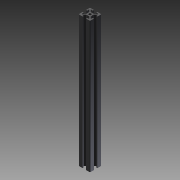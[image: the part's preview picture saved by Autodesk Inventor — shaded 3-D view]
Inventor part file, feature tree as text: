
AUTODESK INVENTOR PART (.ipt)
format: ipt  version: 2011 SP1 (Build 150282100, 282)  size: 185,344 bytes
history: native  units: mm
features: other x7, sketch x2, extrude x1, hole x1
ambient origin geometry x8: Origin, YZ Plane, XZ Plane, XY Plane, X Axis, Y Axis, Z Axis, Center Point
bodies: Solid1 (feature_tree)
feature tree (11):
  extrude  "Extrusion1"  TaperAngle=0.0deg  [1 undecoded]
  hole  "Hole1"  [1 undecoded]
  other  "C1_XY"
  other  "C1_YZ"
  other  "C1_ZX"
  other  "C1_X"
  other  "C1_Y"
  other  "C1_Z"
  other  "C1_Center"
  sketch  "Sketch_75"  dims[d2=4.2mm d3=6.0mm d4=4.0mm d5=2.0mm d6=90.0deg d7=230.0mm d8=0.0mm d9=0.0mm]
  sketch  "Sketch2"  dims[d0=230.0mm d1=0.0mm]
note: 2 required parameter values undecoded (feature->parameter linkage not recoverable at this tier; creation-order binding heuristic only, values carry confidence <= 0.55)
